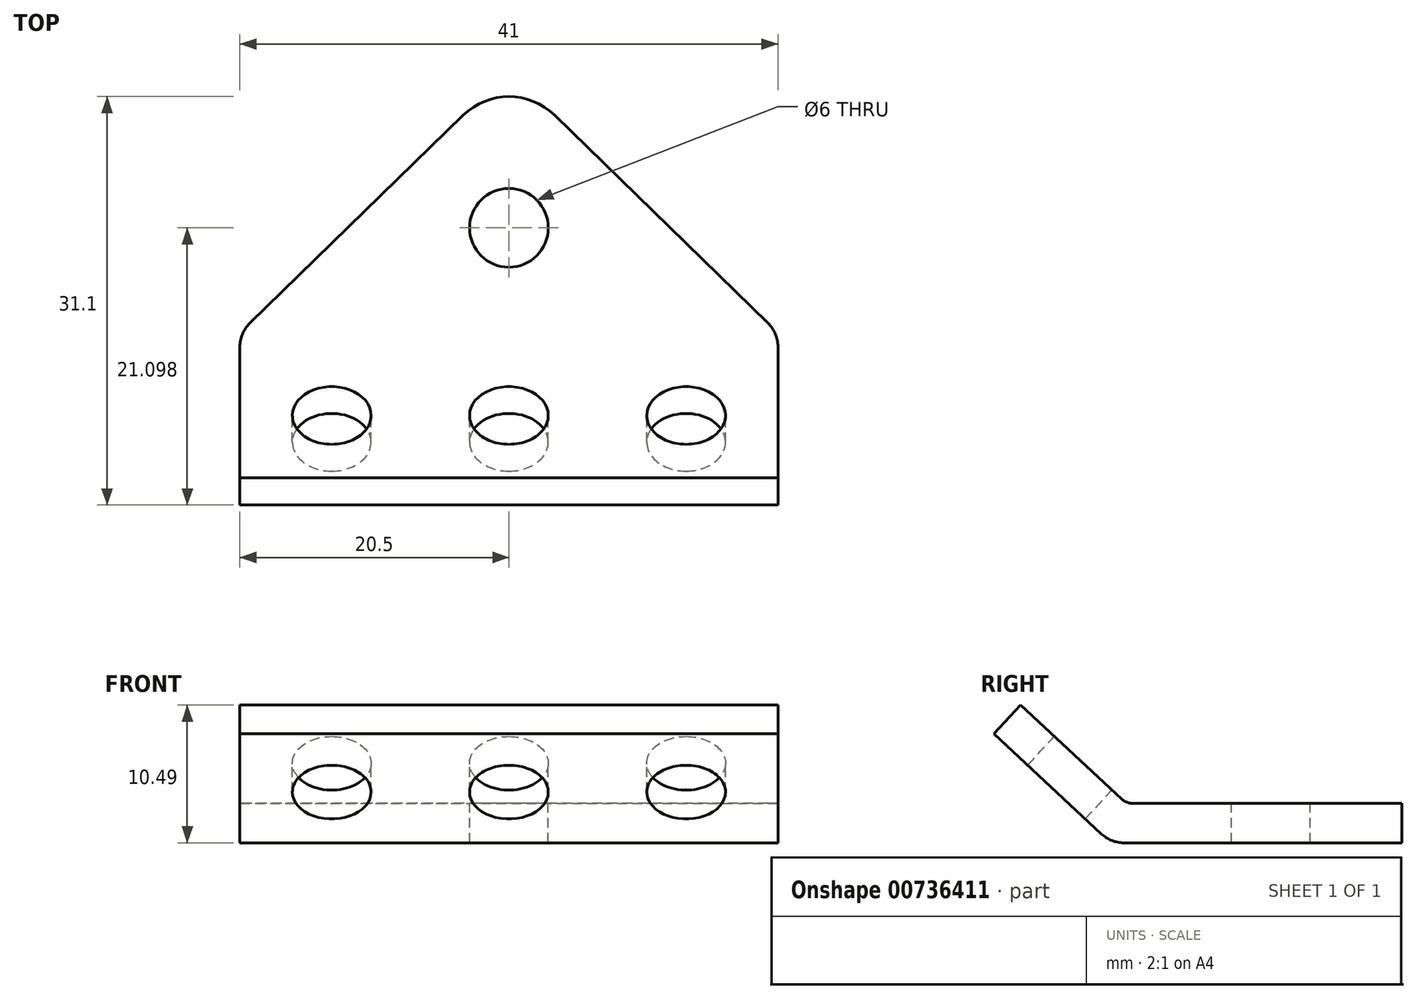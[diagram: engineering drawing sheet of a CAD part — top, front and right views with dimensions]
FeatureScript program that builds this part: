
annotation { "Feature Type Name" : "Feature", "Feature Type Description" : "" }
export const myFeature = defineFeature(function(context is Context, id is Id, definition is map)
    precondition{}
    {
        {
            var Q0;
            Q0=qCreatedBy(makeId("Top.planeOp"),FACE);
            var sketch = newSketch(context, id + "F0", { "sketchPlane" : qUnion([Q0])});
            skLineSegment(sketch, "E0", {"start": v(-3.5, -3.4) * mm, "end": v(-19.75, -19.25) * mm});
            skLineSegment(sketch, "E1", {"start": v(-20.5, -21.04) * mm, "end": v(-20.5, -22.98) * mm});
            skLineSegment(sketch, "E2", {"start": v(-20.5, -22.98) * mm, "end": v(20.5, -22.98) * mm});
            skLineSegment(sketch, "E3", {"start": v(20.5, -22.98) * mm, "end": v(20.5, -21.04) * mm});
            skLineSegment(sketch, "E4", {"start": v(19.75, -19.25) * mm, "end": v(3.5, -3.4) * mm});
            skPoint(sketch, "E5.visualSharp", {"position": v(0, 0) * mm});
            skArc(sketch, "E5.filletArc", {"start": v(3.5, -3.4) * mm, "mid": v(0, -1.98) * mm, "end": v(-3.5, -3.4) * mm});
            skPoint(sketch, "E6.visualSharp", {"position": v(-20.5, -19.98) * mm});
            skArc(sketch, "E6.filletArc", {"start": v(-19.75, -19.25) * mm, "mid": v(-20.3, -20.07) * mm, "end": v(-20.5, -21.04) * mm});
            skPoint(sketch, "E7.visualSharp", {"position": v(20.5, -19.98) * mm});
            skArc(sketch, "E7.filletArc", {"start": v(20.5, -21.04) * mm, "mid": v(20.3, -20.07) * mm, "end": v(19.75, -19.25) * mm});
            skSolve(sketch);
        }
        {
            var Q0;
            Q0=qSketchRegion(id+"F0",true);
            extrude(context, id + "F1", {"entities" : qUnion([Q0]), "depth" : 3 * mm, "offsetDistance" : 25 * mm});
        }
        {
            var Q0;
            Q0=makeQuery(id+"F1.opExtrude","CAP_FACE",FACE,{"disambiguationData":[OSD([sQuery(id+"F0.wireOp",EDGE,"E0"),sQuery(id+"F0.wireOp",EDGE,"E1"),sQuery(id+"F0.wireOp",EDGE,"E2"),sQuery(id+"F0.wireOp",EDGE,"E3"),sQuery(id+"F0.wireOp",EDGE,"E4"),sQuery(id+"F0.wireOp",EDGE,"E5.filletArc"),sQuery(id+"F0.wireOp",EDGE,"E6.filletArc"),sQuery(id+"F0.wireOp",EDGE,"E7.filletArc")])],"isStart":false});
            var sketch = newSketch(context, id + "F2", { "sketchPlane" : qUnion([Q0])});
            skCircle(sketch, "E8", {"center": v(0, -11.98) * mm, "radius": 3 * mm});
            skSolve(sketch);
        }
        {
            var Q0;
            Q0=qSketchRegion(id+"F2",true);
            extrude(context, id + "F3", {"entities" : qUnion([Q0]), "operationType" : NewBodyOperationType.REMOVE, "oppositeDirection" : true, "depth" : 3 * mm, "offsetDistance" : 25 * mm});
        }
        {
            var Q0;
            Q0=makeQuery(id+"F1.opExtrude","SWEPT_FACE",FACE,{"disambiguationData":[OSD([sQuery(id+"F0.wireOp",EDGE,"E1")])]});
            var sketch = newSketch(context, id + "F4", { "sketchPlane" : qUnion([Q0])});
            skLineSegment(sketch, "E9", {"start": v(22.98, 3) * mm, "end": v(31.04, 10.5) * mm});
            skLineSegment(sketch, "E10", {"start": v(31.04, 10.5) * mm, "end": v(33.08, 8.3) * mm});
            skLineSegment(sketch, "E11", {"start": v(33.08, 8.3) * mm, "end": v(24.88, 0.67) * mm});
            skLineSegment(sketch, "E12", {"start": v(23.18, 0) * mm, "end": v(22.98, 0) * mm});
            skPoint(sketch, "E13.visualSharp", {"position": v(24.16, 0) * mm});
            skArc(sketch, "E13.filletArc", {"start": v(23.18, 0) * mm, "mid": v(24.1, 0.17) * mm, "end": v(24.88, 0.67) * mm});
            skSolve(sketch);
        }
        {
            var Q0;
            Q0=makeQuery(id+"F4.imprint","IMPRINT",FACE,{"disambiguationData":[TD([[makeQuery(id+"F4.imprint","IMPRINT",EDGE,{"derivedFrom":sQuery(id+"F4.wireOp",EDGE,"E9")}),-1.0]])]});
            extrude(context, id + "F5", {"entities" : qUnion([Q0]), "operationType" : NewBodyOperationType.ADD, "depth" : -41 * mm, "offsetDistance" : 25 * mm});
        }
        {
            var Q0;
            {var subQ0=sQuery(id+"F0.wireOp",EDGE,"E2");Q0=makeQuery(id+"F5.boolean.opBoolean","MERGE",EDGE,{"derivedFrom":[makeQuery(id+"F1.opExtrude","CAP_EDGE",EDGE,{"disambiguationData":[OSD([subQ0])],"isStart":false}),makeQuery(id+"F5.opExtrude","SWEPT_EDGE",EDGE,{"disambiguationData":[OSD([sQuery(id+"F0.wireOp",EDGE,"E1"),subQ0,sQuery(id+"F4.wireOp",EDGE,"E9")])]})]});}
            fillet(context, id + "F6", {"entities" : qUnion([Q0]), "radius" : 1.25 * mm, "tangentPropagation" : true, "allowEdgeOverflow" : false});
        }
        {
            var Q0;
            Q0=makeQuery(id+"F5.opExtrude","SWEPT_FACE",FACE,{"disambiguationData":[OSD([sQuery(id+"F4.wireOp",EDGE,"E9")])]});
            var sketch = newSketch(context, id + "F7", { "sketchPlane" : qUnion([Q0])});
            skCircle(sketch, "E14", {"center": v(13.5, -23.36) * mm, "radius": 3 * mm});
            skCircle(sketch, "E15", {"center": v(0, -23.36) * mm, "radius": 3 * mm});
            skCircle(sketch, "E16", {"center": v(-13.5, -23.36) * mm, "radius": 3 * mm});
            skSolve(sketch);
        }
        {
            var Q0;
            Q0=qSketchRegion(id+"F7",true);
            extrude(context, id + "F8", {"entities" : qUnion([Q0]), "operationType" : NewBodyOperationType.REMOVE, "oppositeDirection" : true, "depth" : 3 * mm, "offsetDistance" : 25 * mm});
        }
    });
